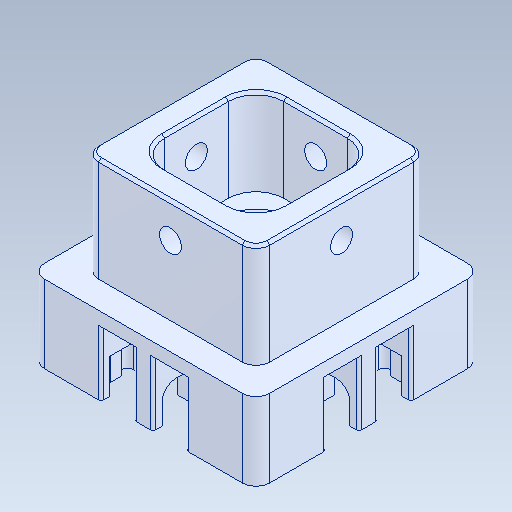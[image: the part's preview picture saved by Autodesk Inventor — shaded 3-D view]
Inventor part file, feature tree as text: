
AUTODESK INVENTOR PART (.ipt)
format: ipt  version: 2020 (Build 240168000, 168)  size: 281,088 bytes
history: native  units: in
note: dims shown in document units (in); Inventor stores cm internally (conversion verified against a paired STEP export)
features: fillet x1
ambient origin geometry x8: Origin, YZ Plane, XZ Plane, XY Plane, X Axis, Y Axis, Z Axis, Center Point
bodies: Solid1 (feature_tree)
feature tree (1):
  fillet  "Fillet6"  [1 undecoded]
note: 1 required parameter value undecoded (feature->parameter linkage not recoverable at this tier; creation-order binding heuristic only, values carry confidence <= 0.55)
